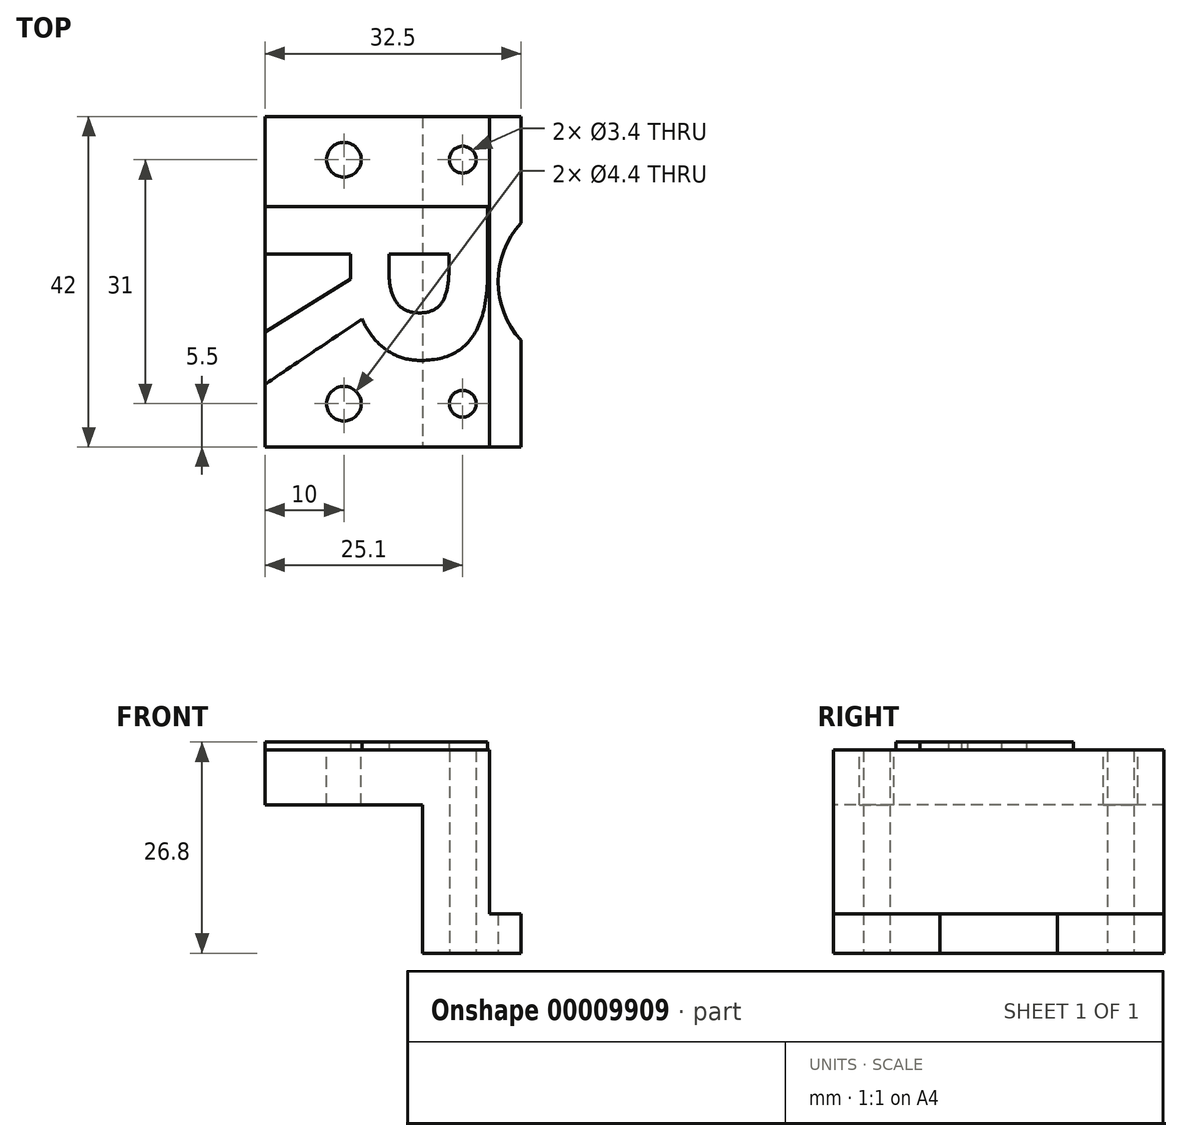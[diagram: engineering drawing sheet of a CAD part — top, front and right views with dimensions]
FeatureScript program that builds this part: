
annotation { "Feature Type Name" : "Feature", "Feature Type Description" : "" }
export const myFeature = defineFeature(function(context is Context, id is Id, definition is map)
    precondition{}
    {
        {
            var Q0;
            Q0=qCreatedBy(makeId("Front.planeOp"),FACE);
            var sketch = newSketch(context, id + "F0", { "sketchPlane" : qUnion([Q0])});
            skLineSegment(sketch, "E0", {"start": v(8.5, 25.8) * mm, "end": v(8.5, 5) * mm});
            skLineSegment(sketch, "E1", {"start": v(8.5, 5) * mm, "end": v(12.5, 5) * mm});
            skLineSegment(sketch, "E2", {"start": v(12.5, 5) * mm, "end": v(12.5, 0) * mm});
            skLineSegment(sketch, "E3", {"start": v(12.5, 0) * mm, "end": v(0, 0) * mm});
            skLineSegment(sketch, "E4", {"start": v(0, 0) * mm, "end": v(0, 25.8) * mm});
            skLineSegment(sketch, "E5", {"start": v(0, 25.8) * mm, "end": v(8.5, 25.8) * mm});
            skSolve(sketch);
        }
        {
            var Q0;
            Q0=qSketchRegion(id+"F0",true);
            extrude(context, id + "F1", {"entities" : qUnion([Q0]), "oppositeDirection" : true, "depth" : 42 * mm});
        }
        {
            var Q0;
            Q0=makeQuery(id+"F1.opExtrude","SWEPT_FACE",FACE,{"disambiguationData":[OSD([sQuery(id+"F0.wireOp",EDGE,"E3")])]});
            var sketch = newSketch(context, id + "F2", { "sketchPlane" : qUnion([Q0])});
            skCircle(sketch, "E6", {"center": v(5.1, -5.5) * mm, "radius": 1.7 * mm});
            skCircle(sketch, "E7", {"center": v(5.1, -36.5) * mm, "radius": 1.7 * mm});
            skCircle(sketch, "E8", {"center": v(20.6, -21) * mm, "radius": 11 * mm});
            skLineSegment(sketch, "E9", {"start": v(0, -21) * mm, "end": v(12.5, -21) * mm, "construction": true});
            skSolve(sketch);
        }
        {
            var Q0;
            Q0=qSketchRegion(id+"F2",true);
            extrude(context, id + "F3", {"entities" : qUnion([Q0]), "operationType" : NewBodyOperationType.REMOVE, "endBound" : BoundingType.THROUGH_ALL, "oppositeDirection" : true, "depth" : 25 * mm});
        }
        {
            var Q0;
            Q0=makeQuery(id+"F1.opExtrude","SWEPT_FACE",FACE,{"disambiguationData":[OSD([sQuery(id+"F0.wireOp",EDGE,"E4")])]});
            var sketch = newSketch(context, id + "F4", { "sketchPlane" : qUnion([Q0])});
            skLineSegment(sketch, "E10.bottom", {"start": v(-42, 25.8) * mm, "end": v(0, 25.8) * mm});
            skLineSegment(sketch, "E10.top", {"start": v(-42, 18.8) * mm, "end": v(0, 18.8) * mm});
            skLineSegment(sketch, "E10.left", {"start": v(-42, 25.8) * mm, "end": v(-42, 18.8) * mm});
            skLineSegment(sketch, "E10.right", {"start": v(0, 25.8) * mm, "end": v(0, 18.8) * mm});
            skSolve(sketch);
        }
        {
            var Q0;
            Q0=qSketchRegion(id+"F4",true);
            extrude(context, id + "F5", {"entities" : qUnion([Q0]), "operationType" : NewBodyOperationType.ADD, "depth" : 20 * mm});
        }
        {
            var Q0;
            Q0=makeQuery(id+"F5.boolean.opBoolean","MERGE",FACE,{"derivedFrom":[makeQuery(id+"F1.opExtrude","SWEPT_FACE",FACE,{"disambiguationData":[OSD([sQuery(id+"F0.wireOp",EDGE,"E5")])]}),makeQuery(id+"F5.opExtrude","SWEPT_FACE",FACE,{"disambiguationData":[OSD([sQuery(id+"F4.wireOp",EDGE,"E10.bottom")])]})]});
            var sketch = newSketch(context, id + "F6", { "sketchPlane" : qUnion([Q0])});
            skCircle(sketch, "E11", {"center": v(-10, 36.5) * mm, "radius": 2.2 * mm});
            skCircle(sketch, "E12", {"center": v(-10, 5.5) * mm, "radius": 2.2 * mm});
            skPoint(sketch, "E13", {"position": v(5.1, 36.5) * mm});
            skPoint(sketch, "E14", {"position": v(5.1, 5.5) * mm});
            skSolve(sketch);
        }
        {
            var Q0;
            Q0=qSketchRegion(id+"F6",true);
            extrude(context, id + "F7", {"entities" : qUnion([Q0]), "operationType" : NewBodyOperationType.REMOVE, "oppositeDirection" : true, "depth" : 25 * mm});
        }
        {
            var Q0;
            Q0=makeQuery(id+"F5.boolean.opBoolean","MERGE",FACE,{"derivedFrom":[makeQuery(id+"F1.opExtrude","SWEPT_FACE",FACE,{"disambiguationData":[OSD([sQuery(id+"F0.wireOp",EDGE,"E5")])]}),makeQuery(id+"F5.opExtrude","SWEPT_FACE",FACE,{"disambiguationData":[OSD([sQuery(id+"F4.wireOp",EDGE,"E10.bottom")])]})]});
            var sketch = newSketch(context, id + "F8", { "sketchPlane" : qUnion([Q0])});
            skText(sketch, "E15", { "text": "R", "fontName": "OpenSans-Bold.ttf"});
            const initialGuessF8  = {"E15": [-0.02, 0.03407, 0, -1, 0.0285]};
            skSetInitialGuess(sketch, initialGuessF8);
            skSolve(sketch);
        }
        {
            var Q0;
            Q0=qSketchRegion(id+"F8",true);
            extrude(context, id + "F9", {"entities" : qUnion([Q0]), "operationType" : NewBodyOperationType.ADD, "depth" : 1 * mm});
        }
    });
